# Revit family: 701305 CIELO MINI WALL-WASHER
name_source: partatom
category: Apparecchi per illuminazione
units: mm (PartAtom-declared; Revit-internal decimal feet)

## family parameters
Basato su piano di lavoro = No
Condiviso = Sì
Mantieni orientamento annotazione = No
Punto di calcolo locali = No
Quota connettore circolare = Usa diametro
Sempre verticale = Sì
Sorgente d'illuminazione = Sì
Taglio con vuoti quando caricato = No
Tipo di parte = Normale

## types (1)
- ALLOY
    Angolo inclinazione = 0.00°
    Available Optics = WALL-WASHER
    Colori = 4000°K    2700°K
    Files diagrammi fotometrici = https://puk.it
    Filtro dei colori = 16777215
    Finish color = STAINLESS STEEL, AISI 316L
    IK Rating = IK10
    IP Rating = IP67
    Ligjt Source = LED
    Material = Hard anodized black aluminium body aisi316l FRONT
    Modello = CIELO MINI WALL-WASHER
    Produttore = PUK
    Prospetto di default = 2023 mm
    URL = https://puk.it
    Variazione temperatura colore lampada con luminosità attenuata = <Nessuno>
    Voltage = 220-240V 50-60Hz
    Wattage = 6W
